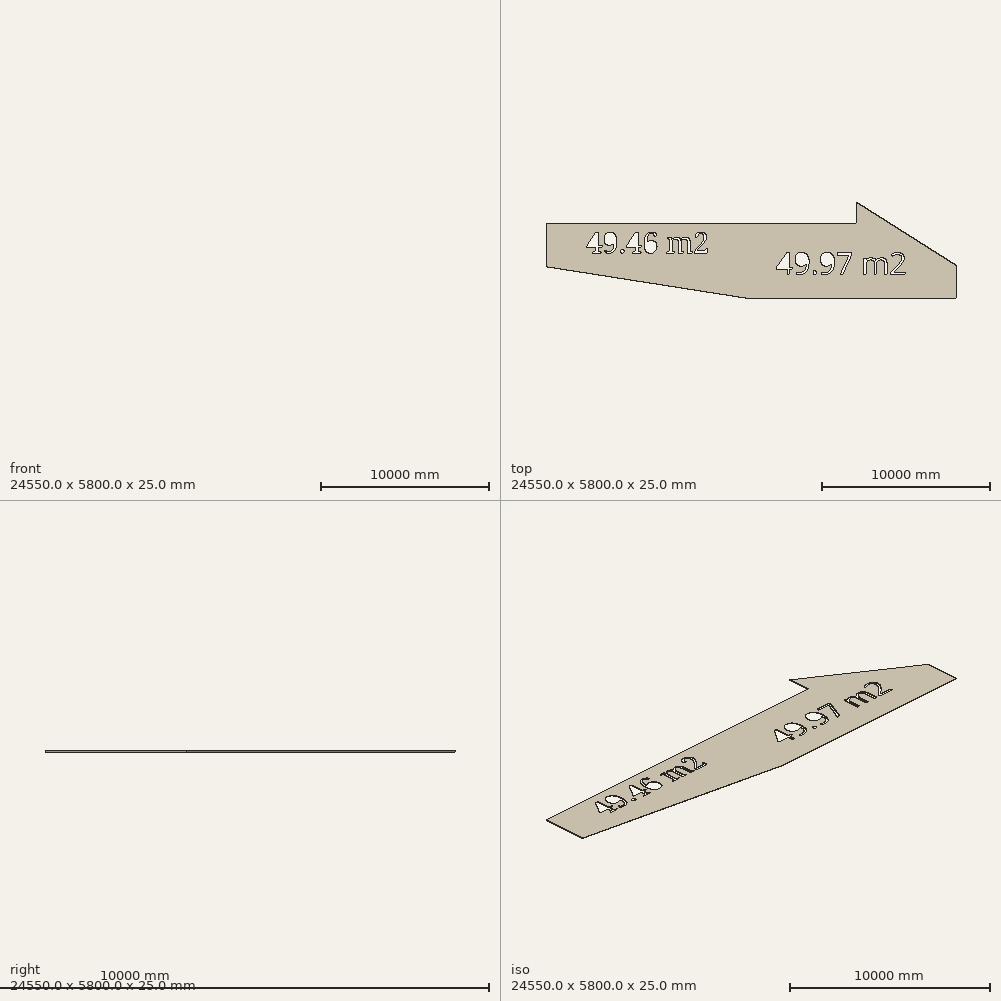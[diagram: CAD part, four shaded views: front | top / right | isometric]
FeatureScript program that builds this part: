
annotation { "Feature Type Name" : "Feature", "Feature Type Description" : "" }
export const myFeature = defineFeature(function(context is Context, id is Id, definition is map)
    precondition{}
    {
        {
            var Q0;
            Q0=qCreatedBy(makeId("Top.planeOp"),FACE);
            var sketch = newSketch(context, id + "F0", { "sketchPlane" : qUnion([Q0])});
            skLineSegment(sketch, "E0", {"start": v(-20459.41, 24022.8) * mm, "end": v(-1909.41, 24022.8) * mm});
            skLineSegment(sketch, "E1", {"start": v(-20459.41, 24022.8) * mm, "end": v(-20459.41, 21447.67) * mm});
            skLineSegment(sketch, "E2", {"start": v(-20459.41, 21447.67) * mm, "end": v(-8209.41, 19522.8) * mm});
            skLineSegment(sketch, "E3", {"start": v(-8209.41, 19522.8) * mm, "end": v(4090.59, 19522.8) * mm});
            skLineSegment(sketch, "E4", {"start": v(4090.59, 19522.8) * mm, "end": v(4090.59, 21522.8) * mm});
            skLineSegment(sketch, "E5", {"start": v(-1909.41, 24022.8) * mm, "end": v(-1909.41, 25322.8) * mm});
            skLineSegment(sketch, "E6", {"start": v(-1909.41, 25322.8) * mm, "end": v(4090.59, 21522.8) * mm});
            skLineSegment(sketch, "E7", {"start": v(-8209.41, 19522.8) * mm, "end": v(-8209.41, 24022.8) * mm});
            skText(sketch, "E8", { "text": "49.46 m2\n", "fontName": "NotoSerif-Regular.ttf"});
            skText(sketch, "E9", { "text": "49.97 m2\n", "fontName": "OpenSans-Regular.ttf"});
            const initialGuessF0  = {"E8": [-18.0784, 22.25834, 1, 0, 1.25276], "E9": [-6.70768, 20.99311, 1, 0, 1.30544]};
            skSetInitialGuess(sketch, initialGuessF0);
            skSolve(sketch);
        }
        {
            var Q0;
            {var subQ0=sQuery(id+"F0.wireOp",EDGE,"E1");Q0=makeQuery(id+"F0.imprint","IMPRINT",FACE,{"disambiguationData":[TD([[makeQuery(id+"F0.imprint","IMPRINT",EDGE,{"derivedFrom":subQ0}),1.0]])]});}
            extrude(context, id + "F1", {"entities" : qUnion([Q0]), "depth" : 25 * mm, "offsetDistance" : 25 * mm});
        }
        {
            var Q0;
            Q0=makeQuery(id+"F0.imprint","IMPRINT",FACE,{"disambiguationData":[TD([[makeQuery(id+"F0.imprint","IMPRINT",EDGE,{"derivedFrom":sQuery(id+"F0.wireOp",EDGE,"E3")}),1.0]])]});
            extrude(context, id + "F2", {"entities" : qUnion([Q0]), "operationType" : NewBodyOperationType.ADD, "depth" : 25 * mm, "offsetDistance" : 25 * mm});
        }
    });
